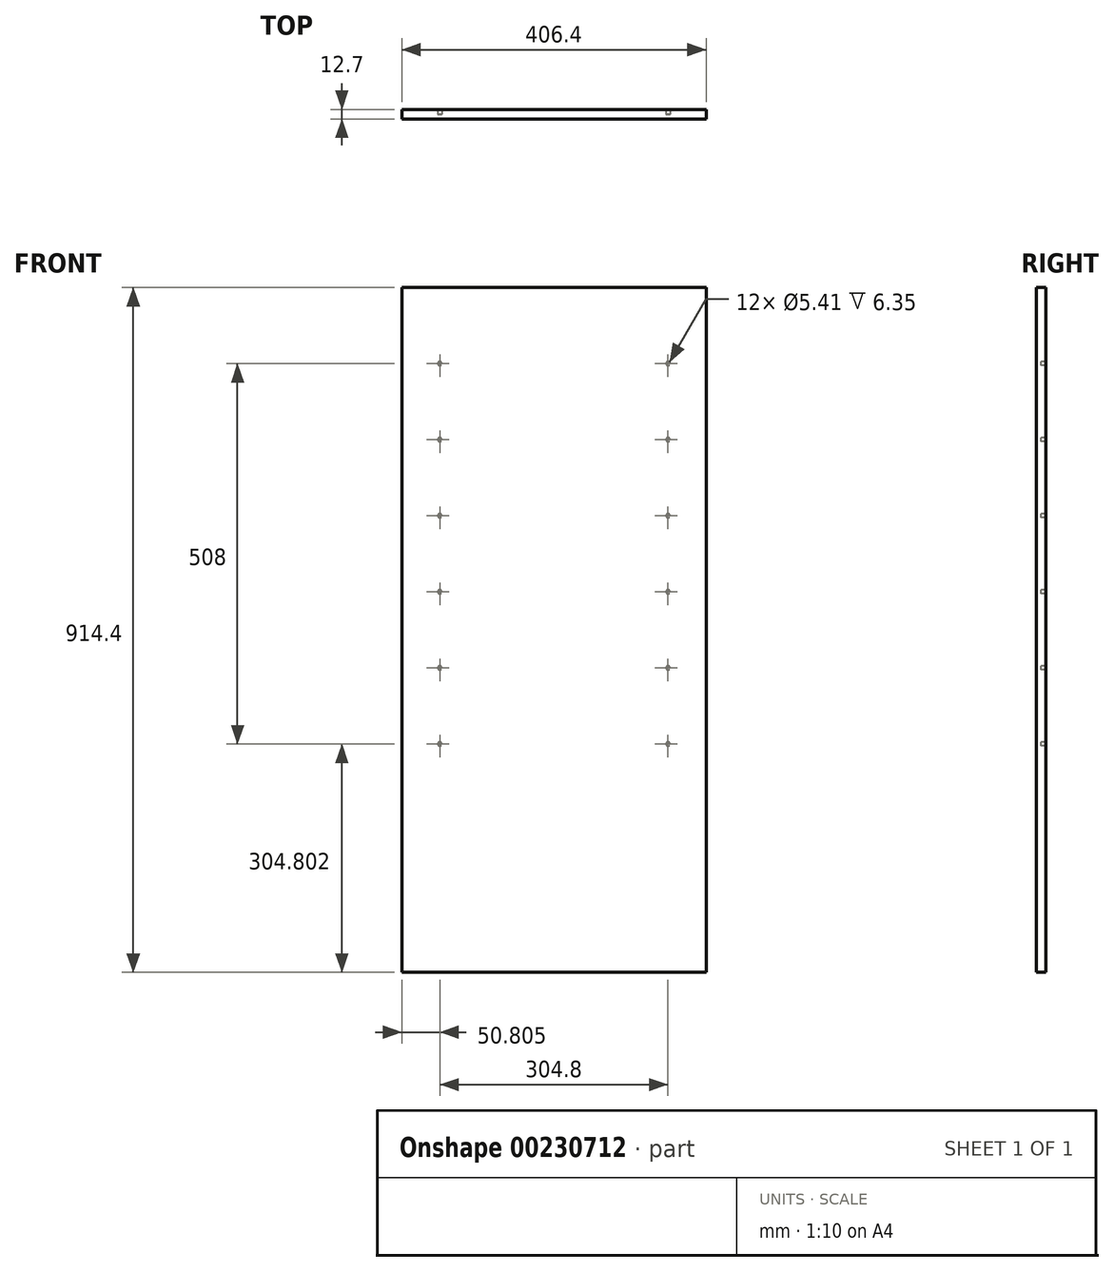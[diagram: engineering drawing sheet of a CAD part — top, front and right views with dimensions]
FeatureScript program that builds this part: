
annotation { "Feature Type Name" : "Feature", "Feature Type Description" : "" }
export const myFeature = defineFeature(function(context is Context, id is Id, definition is map)
    precondition{}
    {
        {
            var Q0;
            Q0=qCreatedBy(makeId("Front.planeOp"),FACE);
            var sketch = newSketch(context, id + "F0", { "sketchPlane" : qUnion([Q0])});
            skLineSegment(sketch, "E0.bottom", {"start": v(-151.68, 682.35) * mm, "end": v(254.72, 682.35) * mm});
            skLineSegment(sketch, "E0.top", {"start": v(-151.68, -232.05) * mm, "end": v(254.72, -232.05) * mm});
            skLineSegment(sketch, "E0.left", {"start": v(-151.68, 682.35) * mm, "end": v(-151.68, -232.05) * mm});
            skLineSegment(sketch, "E0.right", {"start": v(254.72, 682.35) * mm, "end": v(254.72, -232.05) * mm});
            skSolve(sketch);
        }
        {
            var Q0;
            Q0=makeQuery(id+"F0.imprint","IMPRINT",FACE,{"disambiguationData":[TD([[makeQuery(id+"F0.imprint","IMPRINT",EDGE,{"derivedFrom":sQuery(id+"F0.wireOp",EDGE,"E0.bottom")}),-1.0]])]});
            extrude(context, id + "F1", {"entities" : qUnion([Q0]), "depth" : 12.7 * mm, "symmetric" : true});
        }
        {
            var Q0;
            Q0=makeQuery(id+"F0.imprint","IMPRINT",FACE,{"disambiguationData":[TD([[makeQuery(id+"F0.imprint","IMPRINT",EDGE,{"derivedFrom":sQuery(id+"F0.wireOp",EDGE,"E0.bottom")}),-1.0]])]});
            var sketch = newSketch(context, id + "F2", { "sketchPlane" : qUnion([Q0])});
            skPoint(sketch, "E1", {"position": v(-100.88, 72.75) * mm});
            skPoint(sketch, "E2", {"position": v(-100.88, 174.35) * mm});
            skPoint(sketch, "E3", {"position": v(-100.88, 275.95) * mm});
            skPoint(sketch, "E4", {"position": v(-100.88, 377.55) * mm});
            skPoint(sketch, "E5", {"position": v(-100.88, 479.15) * mm});
            skPoint(sketch, "E6", {"position": v(-100.88, 580.75) * mm});
            skPoint(sketch, "E7", {"position": v(203.92, 580.75) * mm});
            skPoint(sketch, "E8", {"position": v(203.92, 479.15) * mm});
            skPoint(sketch, "E9", {"position": v(203.92, 377.55) * mm});
            skPoint(sketch, "E10", {"position": v(203.92, 275.95) * mm});
            skPoint(sketch, "E11", {"position": v(203.92, 174.35) * mm});
            skPoint(sketch, "E12", {"position": v(203.92, 72.75) * mm});
            skSolve(sketch);
        }
        {
            var Q0;
            Q0=sQuery(id+"F2.wireOp",VERTEX,"E6");
            var Q1;
            Q1=sQuery(id+"F2.wireOp",VERTEX,"E5");
            var Q2;
            Q2=sQuery(id+"F2.wireOp",VERTEX,"E4");
            var Q3;
            Q3=sQuery(id+"F2.wireOp",VERTEX,"E3");
            var Q4;
            Q4=sQuery(id+"F2.wireOp",VERTEX,"E2");
            var Q5;
            Q5=sQuery(id+"F2.wireOp",VERTEX,"E1");
            var Q6;
            Q6=sQuery(id+"F2.wireOp",VERTEX,"E12");
            var Q7;
            Q7=sQuery(id+"F2.wireOp",VERTEX,"E11");
            var Q8;
            Q8=sQuery(id+"F2.wireOp",VERTEX,"E10");
            var Q9;
            Q9=sQuery(id+"F2.wireOp",VERTEX,"E9");
            var Q10;
            Q10=sQuery(id+"F2.wireOp",VERTEX,"E8");
            var Q11;
            Q11=sQuery(id+"F2.wireOp",VERTEX,"E7");
            var Q12;
            Q12=makeQuery(id+"F1.opExtrude","SWEPT_BODY",BODY,{"disambiguationData":[OSD([sQuery(id+"F0.wireOp",EDGE,"E0.bottom"),sQuery(id+"F0.wireOp",EDGE,"E0.top"),sQuery(id+"F0.wireOp",EDGE,"E0.left"),sQuery(id+"F0.wireOp",EDGE,"E0.right")])]});
            hole(context, id + "F3", {"style" : HoleStyle.SIMPLE, "endStyle" : HoleEndStyle.BLIND, "standardTappedOrClearance" : lookupTablePath({ "standard" : "ANSI", "size" : "#3 (0.2)", "type" : "Drilled" }), "standardBlindInLast" : lookupTablePath({ "standard" : "ANSI", "size" : "#3", "type" : "Drilled" }), "holeDiameter" : 5.4 * mm, "holeDepth" : 9.52 * mm, "startFromSketch" : true, "locations" : qUnion([Q0, Q1, Q2, Q3, Q4, Q5, Q6, Q7, Q8, Q9, Q10, Q11]), "scope" : qUnion([Q12])});
        }
    });
